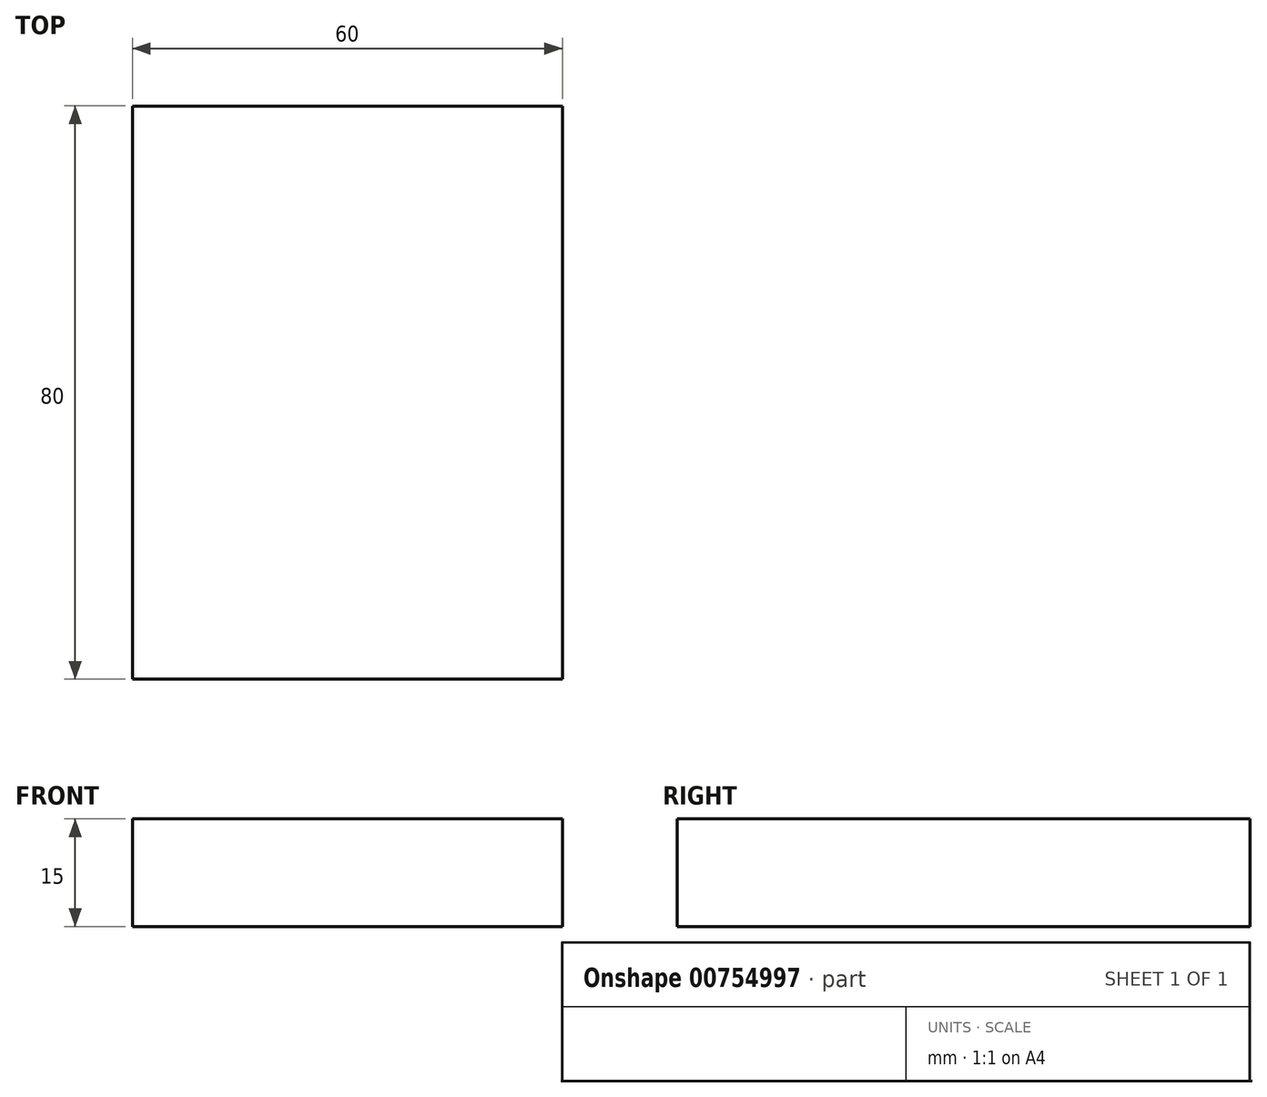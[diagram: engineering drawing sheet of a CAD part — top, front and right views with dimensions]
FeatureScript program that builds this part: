
annotation { "Feature Type Name" : "Feature", "Feature Type Description" : "" }
export const myFeature = defineFeature(function(context is Context, id is Id, definition is map)
    precondition{}
    {
        {
            var Q0;
            Q0=qCreatedBy(makeId("Top.planeOp"),FACE);
            var sketch = newSketch(context, id + "F0", { "sketchPlane" : qUnion([Q0])});
            skLineSegment(sketch, "E0.bottom", {"start": v(-47.31, 56.08) * mm, "end": v(12.69, 56.08) * mm});
            skLineSegment(sketch, "E0.top", {"start": v(-47.31, -23.92) * mm, "end": v(12.69, -23.92) * mm});
            skLineSegment(sketch, "E0.left", {"start": v(-47.31, 56.08) * mm, "end": v(-47.31, -23.92) * mm});
            skLineSegment(sketch, "E0.right", {"start": v(12.69, 56.08) * mm, "end": v(12.69, -23.92) * mm});
            skSolve(sketch);
        }
        {
            var Q0;
            Q0=makeQuery(id+"F0.imprint","IMPRINT",FACE,{"disambiguationData":[TD([[makeQuery(id+"F0.imprint","IMPRINT",EDGE,{"derivedFrom":sQuery(id+"F0.wireOp",EDGE,"E0.bottom")}),-1.0]])]});
            extrude(context, id + "F1", {"entities" : qUnion([Q0]), "depth" : 15 * mm, "offsetDistance" : 25 * mm});
        }
    });
